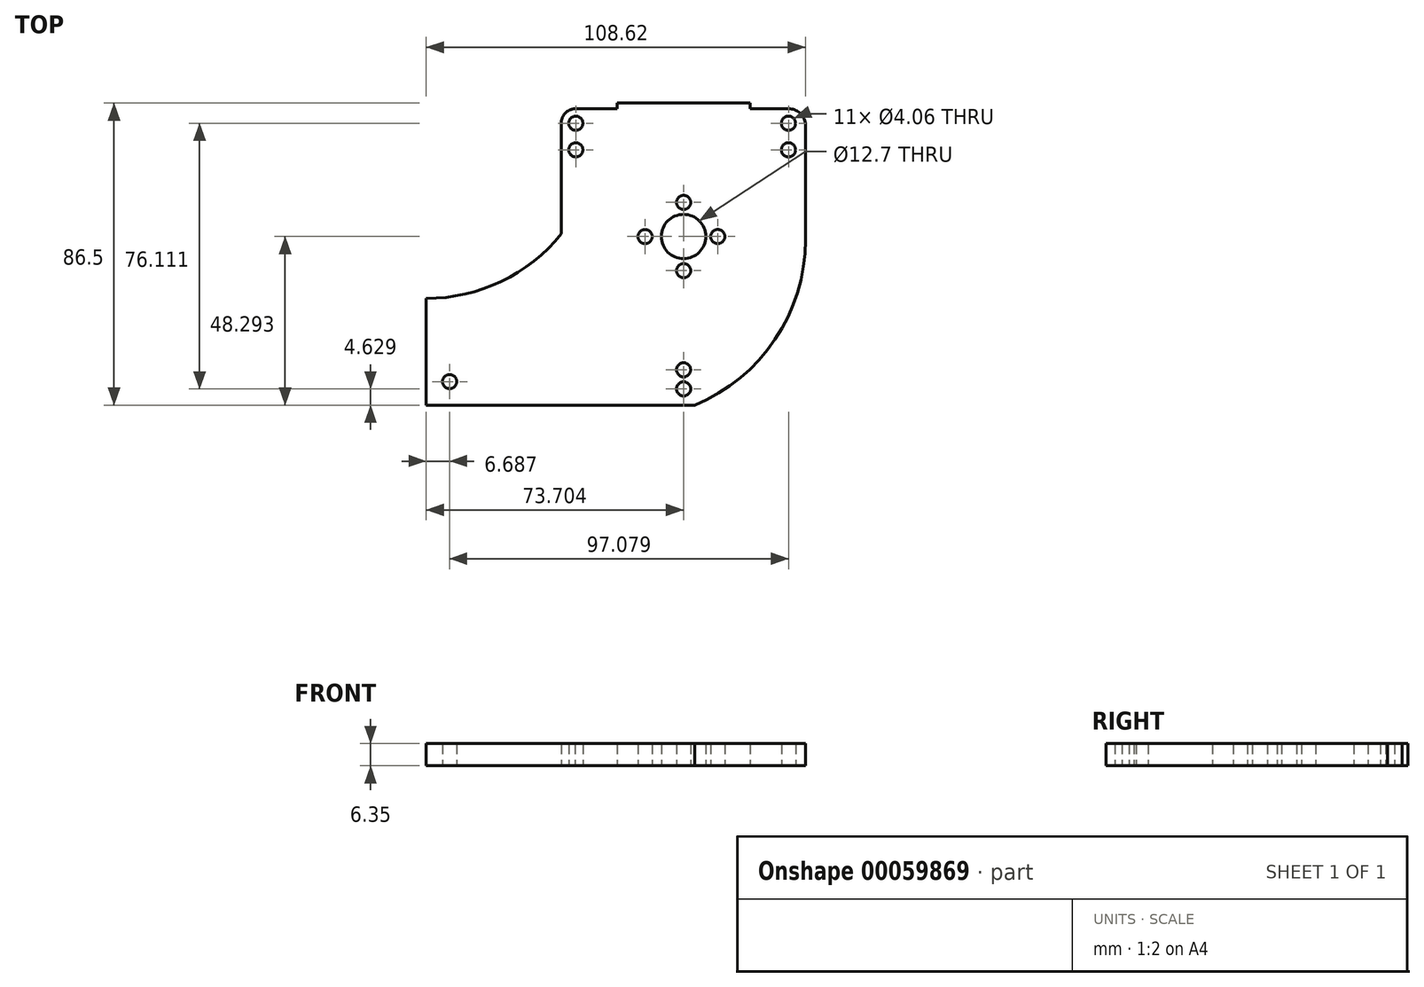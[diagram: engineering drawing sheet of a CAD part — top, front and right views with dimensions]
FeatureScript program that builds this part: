
annotation { "Feature Type Name" : "Feature", "Feature Type Description" : "" }
export const myFeature = defineFeature(function(context is Context, id is Id, definition is map)
    precondition{}
    {
        {
            var Q0;
            Q0=qCreatedBy(makeId("Top.planeOp"),FACE);
            var sketch = newSketch(context, id + "F0", { "sketchPlane" : qUnion([Q0])});
            skPoint(sketch, "E0.endSnap0", {"position": v(-18.33, 34.68) * mm});
            skCircle(sketch, "E1", {"center": v(12.54, -34.84) * mm, "radius": 2.03 * mm});
            skCircle(sketch, "E2", {"center": v(12.54, -40.33) * mm, "radius": 2.03 * mm});
            skLineSegment(sketch, "E3", {"start": v(-61.16, -43.02) * mm, "end": v(-61.16, -36.5) * mm});
            skCircle(sketch, "E4", {"center": v(-54.47, -38.25) * mm, "radius": 2.03 * mm});
            skCircle(sketch, "E5", {"center": v(-18.33, 35.78) * mm, "radius": 2.03 * mm});
            skCircle(sketch, "E6", {"center": v(42.6, 35.78) * mm, "radius": 2.03 * mm});
            skLineSegment(sketch, "E7.top", {"start": v(-61.16, -44.96) * mm, "end": v(15.72, -44.96) * mm});
            skPoint(sketch, "E8.start.orphan", {"position": v(-22.47, 4.1) * mm});
            skPoint(sketch, "E9.start.orphan", {"position": v(-21.53, 41.54) * mm});
            skCircle(sketch, "E10", {"center": v(-18.33, 28.16) * mm, "radius": 2.03 * mm});
            skPoint(sketch, "E11.orphan", {"position": v(47.46, 41.54) * mm});
            skLineSegment(sketch, "E12", {"start": v(-22.47, 4.1) * mm, "end": v(-22.47, 35.78) * mm});
            skPoint(sketch, "E13.end.orphan", {"position": v(42.6, 40.63) * mm});
            skArc(sketch, "E14", {"start": v(15.72, -44.96) * mm, "mid": v(38.79, -26.14) * mm, "end": v(47.46, 2.34) * mm});
            skCircle(sketch, "E15", {"center": v(42.6, 28.16) * mm, "radius": 2.03 * mm});
            skPoint(sketch, "E16.start.orphan", {"position": v(-18.33, 41.54) * mm});
            skArc(sketch, "E17", {"start": v(-18.05, 39.95) * mm, "mid": v(-21.38, 38.64) * mm, "end": v(-22.47, 35.23) * mm});
            skLineSegment(sketch, "E18", {"start": v(-18.6, 39.95) * mm, "end": v(-6.5, 39.95) * mm});
            skArc(sketch, "E19", {"start": v(47.46, 2.34) * mm, "mid": v(47.47, 3.33) * mm, "end": v(47.46, 4.32) * mm});
            skLineSegment(sketch, "E20", {"start": v(-6.5, 41.54) * mm, "end": v(31.6, 41.54) * mm});
            skLineSegment(sketch, "E21", {"start": v(31.6, 41.54) * mm, "end": v(31.6, 39.95) * mm});
            skLineSegment(sketch, "E22", {"start": v(-61.16, -14.4) * mm, "end": v(-61.16, -36.5) * mm});
            skPoint(sketch, "E23.third.point", {"position": v(8.58, 34.83) * mm});
            skLineSegment(sketch, "E24", {"start": v(47.46, 4.32) * mm, "end": v(47.46, 35.78) * mm});
            skLineSegment(sketch, "E25", {"start": v(31.6, 39.95) * mm, "end": v(42.6, 39.95) * mm});
            skArc(sketch, "E26", {"start": v(47.46, 35.78) * mm, "mid": v(45.8, 38.77) * mm, "end": v(42.6, 39.95) * mm});
            skLineSegment(sketch, "E27", {"start": v(47.46, 2.34) * mm, "end": v(47.46, 4.32) * mm});
            skLineSegment(sketch, "E28", {"start": v(-6.5, 39.95) * mm, "end": v(-6.5, 41.54) * mm});
            skLineSegment(sketch, "E7.left", {"start": v(-61.16, -43.02) * mm, "end": v(-61.16, -44.96) * mm});
            skCircle(sketch, "E29", {"center": v(12.54, 3.33) * mm, "radius": 6.35 * mm});
            skCircle(sketch, "E30", {"center": v(12.54, 13.11) * mm, "radius": 2.03 * mm});
            skCircle(sketch, "E31", {"center": v(1.5, 3.31) * mm, "radius": 2.03 * mm});
            skCircle(sketch, "E32", {"center": v(22.32, 3.33) * mm, "radius": 2.03 * mm});
            skCircle(sketch, "E33", {"center": v(12.54, -6.45) * mm, "radius": 2.03 * mm});
            skPoint(sketch, "E23.center.orphan", {"position": v(12.2, 3.31) * mm});
            skPoint(sketch, "E34.orphan", {"position": v(31.6, 35.78) * mm});
            skPoint(sketch, "E35.orphan", {"position": v(15.72, -31.45) * mm});
            skPoint(sketch, "E36.orphan", {"position": v(12.54, -31.6) * mm});
            skPoint(sketch, "E37.left.start.orphan", {"position": v(9.37, -31.6) * mm});
            skPoint(sketch, "E37.right.start.orphan", {"position": v(15.72, -31.6) * mm});
            skPoint(sketch, "E38.start.orphan", {"position": v(12.54, -43.02) * mm});
            skPoint(sketch, "E39.orphan", {"position": v(15.72, -43.02) * mm});
            skPoint(sketch, "E40.start.orphan", {"position": v(9.37, -43.02) * mm});
            skArc(sketch, "E41", {"start": v(-61.16, -14.4) * mm, "mid": v(-39.72, -9.54) * mm, "end": v(-22.47, 4.1) * mm});
            skSolve(sketch);
        }
        {
            var Q0;
            {var subQ0=sQuery(id+"F0.wireOp",EDGE,"8c2d735d-14d7-4c8c-9e6c-6ffa60f7f62a");var subQ1=sQuery(id+"F0.wireOp",EDGE,"4e106400-6662-488a-9453-0d5d5e00814f");var subQ2=makeQuery(id+"F0.imprint","INTERSECT",VERTEX,{"derivedFrom":[subQ1,subQ0]});Q0=makeQuery(id+"F0.imprint","IMPRINT",FACE,{"disambiguationData":[TD([[makeQuery(id+"F0.imprint","IMPRINT",EDGE,{"disambiguationData":[TD([[subQ2,1.0]])],"derivedFrom":subQ1}),-1.0]])]});}
            var Q1;
            {var subQ4=sQuery(id+"F0.wireOp",EDGE,"f1760786-793e-4604-83e6-70300f040a57");var subQ5=sQuery(id+"F0.wireOp",EDGE,"4251fb07-6ccc-4c60-b3af-5654a9b83240");var subQ6=makeQuery(id+"F0.imprint","INTERSECT",VERTEX,{"derivedFrom":[subQ5,subQ4]});Q1=makeQuery(id+"F0.imprint","IMPRINT",FACE,{"disambiguationData":[TD([[makeQuery(id+"F0.imprint","IMPRINT",EDGE,{"disambiguationData":[TD([[subQ6,1.0]])],"derivedFrom":subQ5}),-1.0]])]});}
            var Q2;
            {var subQ0=sQuery(id+"F0.wireOp",EDGE,"6f4dd9dc-e219-4784-b0a4-fd254e89ead9");var subQ1=sQuery(id+"F0.wireOp",EDGE,"d977e9da-4977-4bf3-9238-3f0f7d23d649");var subQ2=makeQuery(id+"F0.imprint","INTERSECT",VERTEX,{"derivedFrom":[subQ1,subQ0]});Q2=makeQuery(id+"F0.imprint","IMPRINT",FACE,{"disambiguationData":[TD([[makeQuery(id+"F0.imprint","IMPRINT",EDGE,{"disambiguationData":[TD([[subQ2,1.0]])],"derivedFrom":subQ1}),1.0]])]});}
            var Q3;
            {var subQ0=sQuery(id+"F0.wireOp",EDGE,"6f4dd9dc-e219-4784-b0a4-fd254e89ead9");var subQ1=makeQuery(id+"F0.imprint","INTERSECT",VERTEX,{"derivedFrom":[sQuery(id+"F0.wireOp",EDGE,"d977e9da-4977-4bf3-9238-3f0f7d23d649"),subQ0]});Q3=makeQuery(id+"F0.imprint","IMPRINT",FACE,{"disambiguationData":[TD([[makeQuery(id+"F0.imprint","IMPRINT",EDGE,{"disambiguationData":[TD([[subQ1,1.0]])],"derivedFrom":subQ0}),1.0]])]});}
            var Q4;
            Q4=makeQuery(id+"F0.imprint","IMPRINT",FACE,{"disambiguationData":[TD([[makeQuery(id+"F0.imprint","IMPRINT",EDGE,{"derivedFrom":sQuery(id+"F0.wireOp",EDGE,"080ca37a-379b-4996-97cf-f76acc6dd72f")}),-1.0]])]});
            var Q5;
            {var subQ5=sQuery(id+"F0.wireOp",EDGE,"d142b7a0-68d0-42f1-aa66-139833cc3c74");var subQ7=sQuery(id+"F0.wireOp",EDGE,"g6liWsM1-4H6Z-jvdt-F6Pt-IPgdiFuZ8wri");var subQ9=makeQuery(id+"F0.imprint","INTERSECT",VERTEX,{"disambiguationData":[OD(1.0)],"derivedFrom":[subQ5,subQ7]});Q5=makeQuery(id+"F0.imprint","IMPRINT",FACE,{"disambiguationData":[TD([[makeQuery(id+"F0.imprint","IMPRINT",EDGE,{"disambiguationData":[TD([[subQ9,-1.0]])],"derivedFrom":subQ5}),-1.0]])]});}
            var Q6;
            {var subQ5=sQuery(id+"F0.wireOp",EDGE,"PJMq3aBf-soeQ-sDjX-Dtg9-O50rWAghBiyd");var subQ6=sQuery(id+"F0.wireOp",EDGE,"b14c26bc-14ff-44f5-a067-41963f7a6e52");var subQ7=makeQuery(id+"F0.imprint","INTERSECT",VERTEX,{"derivedFrom":[subQ6,subQ5]});Q6=makeQuery(id+"F0.imprint","IMPRINT",FACE,{"disambiguationData":[TD([[makeQuery(id+"F0.imprint","IMPRINT",EDGE,{"disambiguationData":[TD([[subQ7,1.0]])],"derivedFrom":subQ6}),-1.0]])]});}
            var Q7;
            {var subQ0=sQuery(id+"F0.wireOp",EDGE,"e1d8f758-f8e8-4c94-a1e5-588ccf0de6c3");var subQ1=sQuery(id+"F0.wireOp",EDGE,"7fa17af4-a1fc-4548-88f0-dd016f7cf8d1");var subQ2=makeQuery(id+"F0.imprint","INTERSECT",VERTEX,{"derivedFrom":[subQ1,subQ0]});Q7=makeQuery(id+"F0.imprint","IMPRINT",FACE,{"disambiguationData":[TD([[makeQuery(id+"F0.imprint","IMPRINT",EDGE,{"disambiguationData":[TD([[subQ2,1.0]])],"derivedFrom":subQ1}),1.0]])]});}
            var Q8;
            {var subQ12=sQuery(id+"F0.wireOp",EDGE,"160f0360-547e-4a7b-a9a4-aa039a1ee5fd");var subQ15=sQuery(id+"F0.wireOp",EDGE,"d142b7a0-68d0-42f1-aa66-139833cc3c74");var subQ16=makeQuery(id+"F0.imprint","INTERSECT",VERTEX,{"derivedFrom":[subQ15,subQ12]});Q8=makeQuery(id+"F0.imprint","IMPRINT",FACE,{"disambiguationData":[TD([[makeQuery(id+"F0.imprint","IMPRINT",EDGE,{"disambiguationData":[TD([[subQ16,-1.0]])],"derivedFrom":subQ15}),-1.0]])]});}
            var Q9;
            {var subQ0=sQuery(id+"F0.wireOp",EDGE,"fcb65023-2698-47d8-abf1-659d14ed80f9");var subQ1=sQuery(id+"F0.wireOp",EDGE,"e4ee2d4d-b378-4754-b236-163ccf585e9b.left");var subQ2=makeQuery(id+"F0.imprint","INTERSECT",VERTEX,{"disambiguationData":[OD(0.0)],"derivedFrom":[subQ1,subQ0]});Q9=makeQuery(id+"F0.imprint","IMPRINT",FACE,{"disambiguationData":[TD([[makeQuery(id+"F0.imprint","IMPRINT",EDGE,{"disambiguationData":[TD([[subQ2,-1.0]])],"derivedFrom":subQ1}),-1.0]])]});}
            var Q10;
            {var subQ0=sQuery(id+"F0.wireOp",EDGE,"e4ee2d4d-b378-4754-b236-163ccf585e9b.top");var subQ1=makeQuery(id+"F0.imprint","INTERSECT",VERTEX,{"derivedFrom":[sQuery(id+"F0.wireOp",EDGE,"89b1195b-aeef-4862-b5a3-332e0bfcf318"),subQ0]});Q10=makeQuery(id+"F0.imprint","IMPRINT",FACE,{"disambiguationData":[TD([[makeQuery(id+"F0.imprint","IMPRINT",EDGE,{"disambiguationData":[TD([[subQ1,1.0]])],"derivedFrom":subQ0}),-1.0]])]});}
            var Q11;
            {var subQ1=sQuery(id+"F0.wireOp",EDGE,"89b1195b-aeef-4862-b5a3-332e0bfcf318");var subQ8=sQuery(id+"F0.wireOp",EDGE,"e4ee2d4d-b378-4754-b236-163ccf585e9b.top");var subQ9=makeQuery(id+"F0.imprint","INTERSECT",VERTEX,{"derivedFrom":[subQ1,subQ8]});Q11=makeQuery(id+"F0.imprint","IMPRINT",FACE,{"disambiguationData":[TD([[makeQuery(id+"F0.imprint","IMPRINT",EDGE,{"disambiguationData":[TD([[subQ9,-1.0]])],"derivedFrom":subQ1}),-1.0]])]});}
            var Q12;
            {var subQ0=sQuery(id+"F0.wireOp",EDGE,"fcb65023-2698-47d8-abf1-659d14ed80f9");var subQ1=sQuery(id+"F0.wireOp",EDGE,"e4ee2d4d-b378-4754-b236-163ccf585e9b.right");var subQ2=makeQuery(id+"F0.imprint","INTERSECT",VERTEX,{"disambiguationData":[OD(0.0)],"derivedFrom":[subQ1,subQ0]});Q12=makeQuery(id+"F0.imprint","IMPRINT",FACE,{"disambiguationData":[TD([[makeQuery(id+"F0.imprint","IMPRINT",EDGE,{"disambiguationData":[TD([[subQ2,-1.0]])],"derivedFrom":subQ1}),1.0]])]});}
            var Q13;
            {var subQ0=sQuery(id+"F0.wireOp",EDGE,"e4ee2d4d-b378-4754-b236-163ccf585e9b.bottom");var subQ1=sQuery(id+"F0.wireOp",EDGE,"89b1195b-aeef-4862-b5a3-332e0bfcf318");var subQ2=makeQuery(id+"F0.imprint","INTERSECT",VERTEX,{"derivedFrom":[subQ1,subQ0]});Q13=makeQuery(id+"F0.imprint","IMPRINT",FACE,{"disambiguationData":[TD([[makeQuery(id+"F0.imprint","IMPRINT",EDGE,{"disambiguationData":[TD([[subQ2,1.0]])],"derivedFrom":subQ1}),-1.0]])]});}
            var Q14;
            {var subQ0=sQuery(id+"F0.wireOp",EDGE,"e4ee2d4d-b378-4754-b236-163ccf585e9b.bottom");var subQ1=sQuery(id+"F0.wireOp",EDGE,"e4ee2d4d-b378-4754-b236-163ccf585e9b.left");var subQ2=makeQuery(id+"F0.imprint","INTERSECT",VERTEX,{"derivedFrom":[subQ1,subQ0]});Q14=makeQuery(id+"F0.imprint","IMPRINT",FACE,{"disambiguationData":[TD([[makeQuery(id+"F0.imprint","IMPRINT",EDGE,{"disambiguationData":[TD([[subQ2,-1.0]])],"derivedFrom":subQ1}),1.0]])]});}
            var Q15;
            {var subQ0=sQuery(id+"F0.wireOp",EDGE,"fcb65023-2698-47d8-abf1-659d14ed80f9");var subQ1=sQuery(id+"F0.wireOp",EDGE,"89b1195b-aeef-4862-b5a3-332e0bfcf318");var subQ2=makeQuery(id+"F0.imprint","INTERSECT",VERTEX,{"derivedFrom":[subQ1,subQ0]});Q15=makeQuery(id+"F0.imprint","IMPRINT",FACE,{"disambiguationData":[TD([[makeQuery(id+"F0.imprint","IMPRINT",EDGE,{"disambiguationData":[TD([[subQ2,-1.0]])],"derivedFrom":subQ1}),1.0]])]});}
            var Q16;
            {var subQ5=sQuery(id+"F0.wireOp",EDGE,"fcb65023-2698-47d8-abf1-659d14ed80f9");var subQ11=sQuery(id+"F0.wireOp",EDGE,"e4ee2d4d-b378-4754-b236-163ccf585e9b.left");var subQ12=makeQuery(id+"F0.imprint","INTERSECT",VERTEX,{"disambiguationData":[OD(0.0)],"derivedFrom":[subQ11,subQ5]});Q16=makeQuery(id+"F0.imprint","IMPRINT",FACE,{"disambiguationData":[TD([[makeQuery(id+"F0.imprint","IMPRINT",EDGE,{"disambiguationData":[TD([[subQ12,-1.0]])],"derivedFrom":subQ11}),1.0]])]});}
            var Q17;
            {var subQ0=sQuery(id+"F0.wireOp",EDGE,"8db0a07e-a23f-4f07-971d-5fa3b9731c29");var subQ1=sQuery(id+"F0.wireOp",EDGE,"89b1195b-aeef-4862-b5a3-332e0bfcf318");var subQ2=makeQuery(id+"F0.imprint","INTERSECT",VERTEX,{"disambiguationData":[OD(0.0)],"derivedFrom":[subQ1,subQ0]});Q17=makeQuery(id+"F0.imprint","IMPRINT",FACE,{"disambiguationData":[TD([[makeQuery(id+"F0.imprint","IMPRINT",EDGE,{"disambiguationData":[TD([[subQ2,-1.0]])],"derivedFrom":subQ1}),1.0]])]});}
            var Q18;
            {var subQ0=sQuery(id+"F0.wireOp",EDGE,"8db0a07e-a23f-4f07-971d-5fa3b9731c29");var subQ1=sQuery(id+"F0.wireOp",EDGE,"89b1195b-aeef-4862-b5a3-332e0bfcf318");var subQ2=makeQuery(id+"F0.imprint","INTERSECT",VERTEX,{"disambiguationData":[OD(0.0)],"derivedFrom":[subQ1,subQ0]});Q18=makeQuery(id+"F0.imprint","IMPRINT",FACE,{"disambiguationData":[TD([[makeQuery(id+"F0.imprint","IMPRINT",EDGE,{"disambiguationData":[TD([[subQ2,-1.0]])],"derivedFrom":subQ1}),-1.0]])]});}
            var Q19;
            {var subQ0=sQuery(id+"F0.wireOp",EDGE,"fcb65023-2698-47d8-abf1-659d14ed80f9");var subQ1=sQuery(id+"F0.wireOp",EDGE,"89b1195b-aeef-4862-b5a3-332e0bfcf318");var subQ2=makeQuery(id+"F0.imprint","INTERSECT",VERTEX,{"derivedFrom":[subQ1,subQ0]});Q19=makeQuery(id+"F0.imprint","IMPRINT",FACE,{"disambiguationData":[TD([[makeQuery(id+"F0.imprint","IMPRINT",EDGE,{"disambiguationData":[TD([[subQ2,-1.0]])],"derivedFrom":subQ1}),-1.0]])]});}
            var Q20;
            Q20=makeQuery(id+"F0.imprint","IMPRINT",FACE,{"disambiguationData":[TD([[makeQuery(id+"F0.imprint","IMPRINT",EDGE,{"derivedFrom":sQuery(id+"F0.wireOp",EDGE,"a69f10e6-8ec3-42cb-bec8-277ba3d33940")}),-1.0]])]});
            var Q21;
            {var subQ0=sQuery(id+"F0.wireOp",EDGE,"YdjP3EYf-HxS2-Y3aN-Tu1t-S4zxLBSjH7YX");var subQ1=sQuery(id+"F0.wireOp",EDGE,"d142b7a0-68d0-42f1-aa66-139833cc3c74");var subQ2=makeQuery(id+"F0.imprint","INTERSECT",VERTEX,{"disambiguationData":[OD(0.0)],"derivedFrom":[subQ1,subQ0]});Q21=makeQuery(id+"F0.imprint","IMPRINT",FACE,{"disambiguationData":[TD([[makeQuery(id+"F0.imprint","IMPRINT",EDGE,{"disambiguationData":[TD([[subQ2,-1.0]])],"derivedFrom":subQ1}),1.0]])]});}
            var Q22;
            {var subQ1=sQuery(id+"F0.wireOp",EDGE,"fcb65023-2698-47d8-abf1-659d14ed80f9");Q22=makeQuery(id+"F0.imprint","IMPRINT",FACE,{"disambiguationData":[TD([[makeQuery(id+"F0.imprint","IMPRINT",EDGE,{"derivedFrom":subQ1}),1.0]])]});}
            var Q23;
            {var subQ3=sQuery(id+"F0.wireOp",EDGE,"PJMq3aBf-soeQ-sDjX-Dtg9-O50rWAghBiyd");var subQ7=sQuery(id+"F0.wireOp",EDGE,"63bc61b3-eb7b-44b8-9829-ea804d6cb8cd");var subQ9=makeQuery(id+"F0.imprint","INTERSECT",VERTEX,{"derivedFrom":[subQ7,subQ3]});Q23=makeQuery(id+"F0.imprint","IMPRINT",FACE,{"disambiguationData":[TD([[makeQuery(id+"F0.imprint","IMPRINT",EDGE,{"disambiguationData":[TD([[subQ9,1.0]])],"derivedFrom":subQ7}),-1.0]])]});}
            var Q24;
            {var subQ0=sQuery(id+"F0.wireOp",EDGE,"f3edaa75-214d-425a-ab57-1709955d2711");var subQ2=sQuery(id+"F0.wireOp",EDGE,"63bc61b3-eb7b-44b8-9829-ea804d6cb8cd");var subQ3=makeQuery(id+"F0.imprint","INTERSECT",VERTEX,{"disambiguationData":[OD(0.0)],"derivedFrom":[subQ2,subQ0]});Q24=makeQuery(id+"F0.imprint","IMPRINT",FACE,{"disambiguationData":[TD([[makeQuery(id+"F0.imprint","IMPRINT",EDGE,{"disambiguationData":[TD([[subQ3,-1.0]])],"derivedFrom":subQ2}),-1.0]])]});}
            var Q25;
            {var subQ0=sQuery(id+"F0.wireOp",EDGE,"YdjP3EYf-HxS2-Y3aN-Tu1t-S4zxLBSjH7YX");Q25=makeQuery(id+"F0.imprint","IMPRINT",FACE,{"disambiguationData":[TD([[makeQuery(id+"F0.imprint","IMPRINT",EDGE,{"derivedFrom":subQ0}),-1.0]])]});}
            var Q26;
            {var subQ1=sQuery(id+"F0.wireOp",EDGE,"fcb65023-2698-47d8-abf1-659d14ed80f9");Q26=makeQuery(id+"F0.imprint","IMPRINT",FACE,{"disambiguationData":[TD([[makeQuery(id+"F0.imprint","IMPRINT",EDGE,{"derivedFrom":subQ1}),-1.0]])]});}
            var Q27;
            {var subQ0=sQuery(id+"F0.wireOp",EDGE,"rbOIPqF2-cMIc-KdIQ-13li-LU4bAKKfAOrR");Q27=makeQuery(id+"F0.imprint","IMPRINT",FACE,{"disambiguationData":[TD([[makeQuery(id+"F0.imprint","IMPRINT",EDGE,{"derivedFrom":subQ0}),1.0]])]});}
            var Q28;
            {var subQ0=sQuery(id+"F0.wireOp",EDGE,"d3b900f8-6608-4e03-b776-9779dfdf90f4");var subQ1=sQuery(id+"F0.wireOp",EDGE,"680942e8-7e09-4fca-a324-80caf94b3383");var subQ2=makeQuery(id+"F0.imprint","INTERSECT",VERTEX,{"disambiguationData":[OD(0.0)],"derivedFrom":[subQ1,subQ0]});Q28=makeQuery(id+"F0.imprint","IMPRINT",FACE,{"disambiguationData":[TD([[makeQuery(id+"F0.imprint","IMPRINT",EDGE,{"disambiguationData":[TD([[subQ2,1.0]])],"derivedFrom":subQ1}),-1.0]])]});}
            var Q29;
            {var subQ2=sQuery(id+"F0.wireOp",EDGE,"af0bd3a2-90fb-4c99-b38e-c83de925c3d3");var subQ6=makeQuery(id+"F0.imprint","INTERSECT",VERTEX,{"disambiguationData":[OD(1.0)],"derivedFrom":[subQ2,sQuery(id+"F0.wireOp",EDGE,"g6liWsM1-4H6Z-jvdt-F6Pt-IPgdiFuZ8wri")]});Q29=makeQuery(id+"F0.imprint","IMPRINT",FACE,{"disambiguationData":[TD([[makeQuery(id+"F0.imprint","IMPRINT",EDGE,{"disambiguationData":[TD([[subQ6,1.0]])],"derivedFrom":subQ2}),-1.0]])]});}
            var Q30;
            {var subQ0=sQuery(id+"F0.wireOp",EDGE,"g6liWsM1-4H6Z-jvdt-F6Pt-IPgdiFuZ8wri");var subQ1=sQuery(id+"F0.wireOp",EDGE,"af0bd3a2-90fb-4c99-b38e-c83de925c3d3");var subQ2=makeQuery(id+"F0.imprint","INTERSECT",VERTEX,{"disambiguationData":[OD(1.0)],"derivedFrom":[subQ1,subQ0]});Q30=makeQuery(id+"F0.imprint","IMPRINT",FACE,{"disambiguationData":[TD([[makeQuery(id+"F0.imprint","IMPRINT",EDGE,{"disambiguationData":[TD([[subQ2,1.0]])],"derivedFrom":subQ1}),1.0]])]});}
            var Q31;
            {var subQ0=sQuery(id+"F0.wireOp",EDGE,"g6liWsM1-4H6Z-jvdt-F6Pt-IPgdiFuZ8wri");var subQ1=sQuery(id+"F0.wireOp",EDGE,"af0bd3a2-90fb-4c99-b38e-c83de925c3d3");var subQ2=makeQuery(id+"F0.imprint","INTERSECT",VERTEX,{"disambiguationData":[OD(0.0)],"derivedFrom":[subQ1,subQ0]});Q31=makeQuery(id+"F0.imprint","IMPRINT",FACE,{"disambiguationData":[TD([[makeQuery(id+"F0.imprint","IMPRINT",EDGE,{"disambiguationData":[TD([[subQ2,-1.0]])],"derivedFrom":subQ1}),1.0]])]});}
            var Q32;
            {var subQ4=sQuery(id+"F0.wireOp",EDGE,"2b21c116-94b0-4f92-9be9-82b28d9caaf5");Q32=makeQuery(id+"F0.imprint","IMPRINT",FACE,{"disambiguationData":[TD([[makeQuery(id+"F0.imprint","IMPRINT",EDGE,{"derivedFrom":subQ4}),1.0]])]});}
            var Q33;
            Q33=makeQuery(id+"F0.imprint","IMPRINT",FACE,{"disambiguationData":[TD([[makeQuery(id+"F0.imprint","IMPRINT",EDGE,{"derivedFrom":sQuery(id+"F0.wireOp",EDGE,"E3")}),-1.0]])]});
            var Q34;
            Q34=makeQuery(id+"F0.imprint","IMPRINT",FACE,{"disambiguationData":[TD([[makeQuery(id+"F0.imprint","IMPRINT",EDGE,{"derivedFrom":sQuery(id+"F0.wireOp",EDGE,"E10")}),-1.0]])]});
            var Q35;
            {var subQ0=sQuery(id+"F0.wireOp",EDGE,"E20");Q35=makeQuery(id+"F0.imprint","IMPRINT",FACE,{"disambiguationData":[TD([[makeQuery(id+"F0.imprint","IMPRINT",EDGE,{"derivedFrom":subQ0}),-1.0]])]});}
            var Q36;
            Q36=makeQuery(id+"F0.imprint","IMPRINT",FACE,{"disambiguationData":[TD([[makeQuery(id+"F0.imprint","IMPRINT",EDGE,{"derivedFrom":sQuery(id+"F0.wireOp",EDGE,"E15")}),-1.0]])]});
            var Q37;
            Q37=makeQuery(id+"F0.imprint","IMPRINT",FACE,{"disambiguationData":[TD([[makeQuery(id+"F0.imprint","IMPRINT",EDGE,{"derivedFrom":sQuery(id+"F0.wireOp",EDGE,"E7.top")}),1.0]])]});
            var Q38;
            {var subQ6=sQuery(id+"F0.wireOp",EDGE,"E37.left");Q38=makeQuery(id+"F0.imprint","IMPRINT",FACE,{"disambiguationData":[TD([[makeQuery(id+"F0.imprint","IMPRINT",EDGE,{"derivedFrom":subQ6}),1.0]])]});}
            var Q39;
            {var subQ4=sQuery(id+"F0.wireOp",EDGE,"E37.right");Q39=makeQuery(id+"F0.imprint","IMPRINT",FACE,{"disambiguationData":[TD([[makeQuery(id+"F0.imprint","IMPRINT",EDGE,{"derivedFrom":subQ4}),-1.0]])]});}
            extrude(context, id + "F1", {"entities" : qUnion([Q0, Q1, Q2, Q3, Q4, Q5, Q6, Q7, Q8, Q9, Q10, Q11, Q12, Q13, Q14, Q15, Q16, Q17, Q18, Q19, Q20, Q21, Q22, Q23, Q24, Q25, Q26, Q27, Q28, Q29, Q30, Q31, Q32, Q33, Q34, Q35, Q36, Q37, Q38, Q39]), "depth" : 6.35 * mm});
        }
    });
